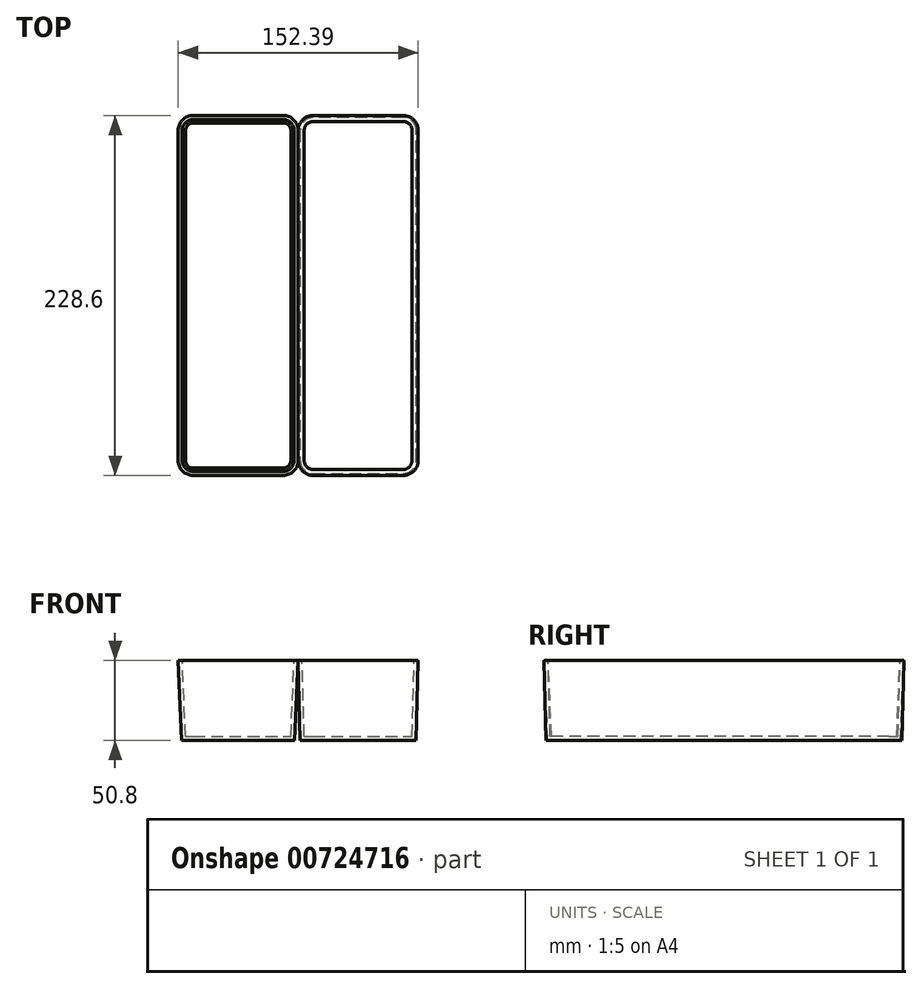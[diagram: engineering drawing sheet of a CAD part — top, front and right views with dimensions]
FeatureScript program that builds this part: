
annotation { "Feature Type Name" : "Feature", "Feature Type Description" : "" }
export const myFeature = defineFeature(function(context is Context, id is Id, definition is map)
    precondition{}
    {
        {
            var Q0;
            Q0=qCreatedBy(makeId("Top.planeOp"),FACE);
            var sketch = newSketch(context, id + "F0", { "sketchPlane" : qUnion([Q0])});
            skLineSegment(sketch, "E0.bottom", {"start": v(9.52, 0) * mm, "end": v(66.67, 0) * mm});
            skLineSegment(sketch, "E0.top", {"start": v(9.52, 228.6) * mm, "end": v(66.67, 228.6) * mm});
            skLineSegment(sketch, "E0.left", {"start": v(0, 9.53) * mm, "end": v(0, 219.08) * mm});
            skLineSegment(sketch, "E0.right", {"start": v(76.2, 9.53) * mm, "end": v(76.2, 219.08) * mm});
            skPoint(sketch, "E1.visualSharp", {"position": v(0, 0) * mm});
            skArc(sketch, "E1.filletArc", {"start": v(0, 9.52) * mm, "mid": v(2.79, 2.79) * mm, "end": v(9.52, 0) * mm});
            skPoint(sketch, "E2.visualSharp", {"position": v(76.2, 0) * mm});
            skArc(sketch, "E2.filletArc", {"start": v(66.67, 0) * mm, "mid": v(73.41, 2.79) * mm, "end": v(76.2, 9.53) * mm});
            skPoint(sketch, "E3.visualSharp", {"position": v(0, 228.6) * mm});
            skArc(sketch, "E3.filletArc", {"start": v(9.52, 228.6) * mm, "mid": v(2.79, 225.81) * mm, "end": v(0, 219.08) * mm});
            skPoint(sketch, "E4.visualSharp", {"position": v(76.2, 228.6) * mm});
            skArc(sketch, "E4.filletArc", {"start": v(76.2, 219.08) * mm, "mid": v(73.41, 225.81) * mm, "end": v(66.67, 228.6) * mm});
            skLineSegment(sketch, "E5", {"start": v(76.2, 0) * mm, "end": v(76.2, 248) * mm, "construction": true});
            skSolve(sketch);
        }
        {
            var Q0;
            Q0=makeQuery(id+"F0.imprint","IMPRINT",FACE,{"disambiguationData":[TD([[makeQuery(id+"F0.imprint","IMPRINT",EDGE,{"derivedFrom":sQuery(id+"F0.wireOp",EDGE,"E0.bottom")}),1.0]])]});
            extrude(context, id + "F1", {"entities" : qUnion([Q0]), "oppositeDirection" : true, "depth" : 50.8 * mm, "offsetDistance" : 25.4 * mm, "hasDraft" : true, "draftAngle" : 1.5 * degree, "draftPullDirection" : true});
        }
        {
            var Q0;
            Q0=makeQuery(id+"F1.opExtrude","CAP_FACE",FACE,{"disambiguationData":[OSD([sQuery(id+"F0.wireOp",EDGE,"E0.bottom"),sQuery(id+"F0.wireOp",EDGE,"E0.top"),sQuery(id+"F0.wireOp",EDGE,"E0.left"),sQuery(id+"F0.wireOp",EDGE,"E0.right"),sQuery(id+"F0.wireOp",EDGE,"E1.filletArc"),sQuery(id+"F0.wireOp",EDGE,"E2.filletArc"),sQuery(id+"F0.wireOp",EDGE,"E3.filletArc"),sQuery(id+"F0.wireOp",EDGE,"E4.filletArc")])],"isStart":true});
            shell(context, id + "F2", {"entities" : qUnion([Q0]), "thickness" : 2.54 * mm});
        }
        {
            var Q0;
            Q0=makeQuery(id+"F1.opExtrude","CAP_EDGE",EDGE,{"disambiguationData":[OSD([sQuery(id+"F0.wireOp",EDGE,"E0.bottom")])],"isStart":true});
            var Q1;
            Q1=makeQuery(id+"F1.opExtrude","CAP_EDGE",EDGE,{"disambiguationData":[OSD([sQuery(id+"F0.wireOp",EDGE,"E2.filletArc")])],"isStart":true});
            var Q2;
            Q2=makeQuery(id+"F1.opExtrude","CAP_EDGE",EDGE,{"disambiguationData":[OSD([sQuery(id+"F0.wireOp",EDGE,"E0.right")])],"isStart":true});
            var Q3;
            Q3=makeQuery(id+"F1.opExtrude","CAP_EDGE",EDGE,{"disambiguationData":[OSD([sQuery(id+"F0.wireOp",EDGE,"E1.filletArc")])],"isStart":true});
            var Q4;
            Q4=makeQuery(id+"F1.opExtrude","CAP_EDGE",EDGE,{"disambiguationData":[OSD([sQuery(id+"F0.wireOp",EDGE,"E0.left")])],"isStart":true});
            var Q5;
            Q5=makeQuery(id+"F1.opExtrude","CAP_EDGE",EDGE,{"disambiguationData":[OSD([sQuery(id+"F0.wireOp",EDGE,"E3.filletArc")])],"isStart":true});
            var Q6;
            Q6=makeQuery(id+"F1.opExtrude","CAP_EDGE",EDGE,{"disambiguationData":[OSD([sQuery(id+"F0.wireOp",EDGE,"E0.top")])],"isStart":true});
            var Q7;
            Q7=makeQuery(id+"F1.opExtrude","CAP_EDGE",EDGE,{"disambiguationData":[OSD([sQuery(id+"F0.wireOp",EDGE,"E4.filletArc")])],"isStart":true});
            var Q8;
            {var subQ0=sQuery(id+"F0.wireOp",EDGE,"E0.bottom");Q8=makeQuery(id+"F2.opShell","OFFSET_EDGE",EDGE,{"disambiguationData":[OSD([subQ0]),TDD([makeQuery(id+"F1.opExtrude","CAP_EDGE",EDGE,{"disambiguationData":[OSD([subQ0])],"isStart":true})])]});}
            var Q9;
            {var subQ0=sQuery(id+"F0.wireOp",EDGE,"E0.right");Q9=makeQuery(id+"F2.opShell","OFFSET_EDGE",EDGE,{"disambiguationData":[OSD([subQ0]),TDD([makeQuery(id+"F1.opExtrude","CAP_EDGE",EDGE,{"disambiguationData":[OSD([subQ0])],"isStart":true})])]});}
            var Q10;
            {var subQ0=sQuery(id+"F0.wireOp",EDGE,"E0.top");Q10=makeQuery(id+"F2.opShell","OFFSET_EDGE",EDGE,{"disambiguationData":[OSD([subQ0]),TDD([makeQuery(id+"F1.opExtrude","CAP_EDGE",EDGE,{"disambiguationData":[OSD([subQ0])],"isStart":true})])]});}
            var Q11;
            {var subQ0=sQuery(id+"F0.wireOp",EDGE,"E0.left");Q11=makeQuery(id+"F2.opShell","OFFSET_EDGE",EDGE,{"disambiguationData":[OSD([subQ0]),TDD([makeQuery(id+"F1.opExtrude","CAP_EDGE",EDGE,{"disambiguationData":[OSD([subQ0])],"isStart":true})])]});}
            var Q12;
            Q12=makeQuery(id+"F2.opShell","OFFSET_EDGE",EDGE,{"disambiguationData":[OSD([sQuery(id+"F0.wireOp",EDGE,"E0.right"),sQuery(id+"F0.wireOp",EDGE,"E2.filletArc")])]});
            fillet(context, id + "F3", {"entities" : qUnion([Q0, Q1, Q2, Q3, Q4, Q5, Q6, Q7, Q8, Q9, Q10, Q11, Q12]), "radius" : 0.5 * mm, "tangentPropagation" : true, "allowEdgeOverflow" : false});
        }
        {
            var Q0;
            Q0=qCreatedBy(makeId("Top.planeOp"),FACE);
            var sketch = newSketch(context, id + "F4", { "sketchPlane" : qUnion([Q0])});
            skLineSegment(sketch, "E6.bottom", {"start": v(-66.68, 0) * mm, "end": v(-9.53, 0) * mm});
            skLineSegment(sketch, "E6.top", {"start": v(-66.68, 228.6) * mm, "end": v(-9.53, 228.6) * mm});
            skLineSegment(sketch, "E6.left", {"start": v(-76.2, 9.52) * mm, "end": v(-76.2, 219.08) * mm});
            skLineSegment(sketch, "E6.right", {"start": v(0, 9.52) * mm, "end": v(0, 219.08) * mm});
            skPoint(sketch, "E7.visualSharp", {"position": v(-76.2, 0) * mm});
            skArc(sketch, "E7.filletArc", {"start": v(-76.2, 9.52) * mm, "mid": v(-73.41, 2.79) * mm, "end": v(-66.68, 0) * mm});
            skPoint(sketch, "E8.visualSharp", {"position": v(0, 0) * mm});
            skArc(sketch, "E8.filletArc", {"start": v(-9.53, 0) * mm, "mid": v(-2.79, 2.79) * mm, "end": v(0, 9.52) * mm});
            skPoint(sketch, "E9.visualSharp", {"position": v(-76.2, 228.6) * mm});
            skArc(sketch, "E9.filletArc", {"start": v(-66.68, 228.6) * mm, "mid": v(-73.41, 225.81) * mm, "end": v(-76.2, 219.08) * mm});
            skPoint(sketch, "E10.visualSharp", {"position": v(0, 228.6) * mm});
            skArc(sketch, "E10.filletArc", {"start": v(0, 219.08) * mm, "mid": v(-2.79, 225.81) * mm, "end": v(-9.53, 228.6) * mm});
            skSolve(sketch);
        }
        {
            var Q0;
            Q0=makeQuery(id+"F4.imprint","IMPRINT",FACE,{"disambiguationData":[TD([[makeQuery(id+"F4.imprint","IMPRINT",EDGE,{"derivedFrom":sQuery(id+"F4.wireOp",EDGE,"E6.bottom")}),1.0]])]});
            extrude(context, id + "F5", {"entities" : qUnion([Q0]), "oppositeDirection" : true, "depth" : 50.8 * mm, "offsetDistance" : 25.4 * mm, "hasDraft" : true, "draftAngle" : 2.5 * degree, "draftPullDirection" : true});
        }
        {
            var Q0;
            Q0=makeQuery(id+"F5.opExtrude","CAP_FACE",FACE,{"disambiguationData":[OSD([sQuery(id+"F4.wireOp",EDGE,"E6.bottom"),sQuery(id+"F4.wireOp",EDGE,"E6.top"),sQuery(id+"F4.wireOp",EDGE,"E6.left"),sQuery(id+"F4.wireOp",EDGE,"E6.right"),sQuery(id+"F4.wireOp",EDGE,"E7.filletArc"),sQuery(id+"F4.wireOp",EDGE,"E8.filletArc"),sQuery(id+"F4.wireOp",EDGE,"E9.filletArc"),sQuery(id+"F4.wireOp",EDGE,"E10.filletArc")])],"isStart":true});
            shell(context, id + "F6", {"entities" : qUnion([Q0]), "thickness" : 2.54 * mm});
        }
    });
